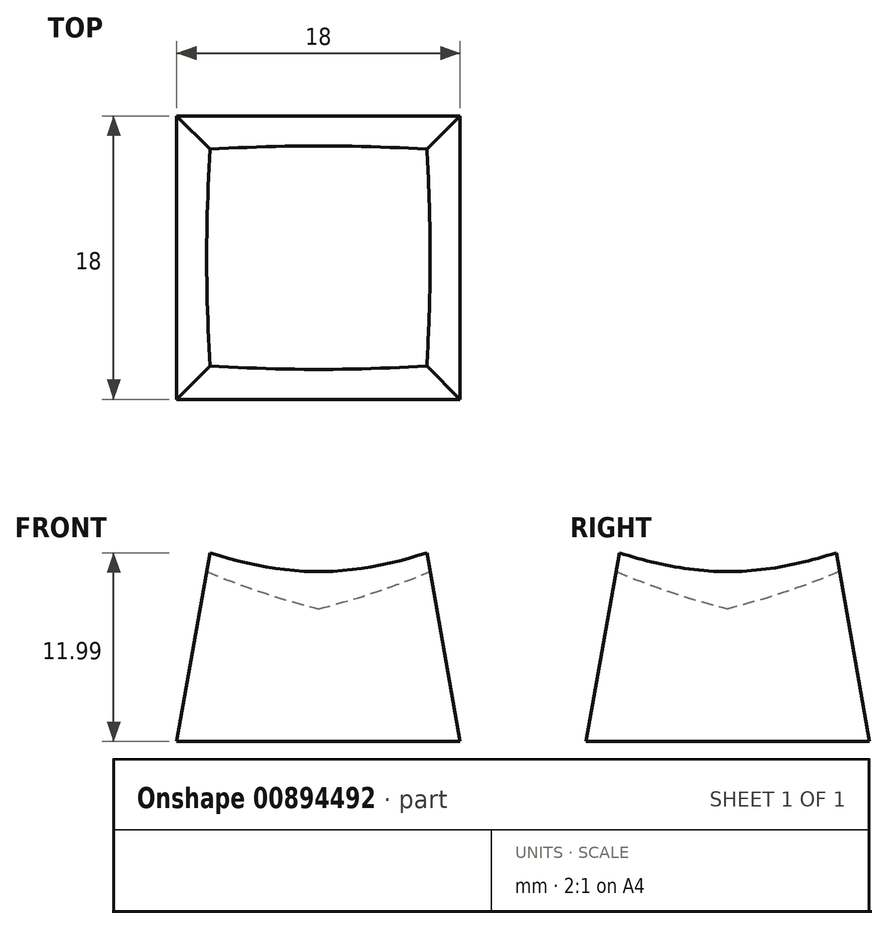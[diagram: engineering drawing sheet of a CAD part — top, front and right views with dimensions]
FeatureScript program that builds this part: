
annotation { "Feature Type Name" : "Feature", "Feature Type Description" : "" }
export const myFeature = defineFeature(function(context is Context, id is Id, definition is map)
    precondition{}
    {
        {
            var Q0;
            Q0=qCreatedBy(makeId("Top.planeOp"),FACE);
            var sketch = newSketch(context, id + "F0", { "sketchPlane" : qUnion([Q0])});
            skLineSegment(sketch, "E0.bottom", {"start": v(-9, 9) * mm, "end": v(9, 9) * mm});
            skLineSegment(sketch, "E0.top", {"start": v(-9, -9) * mm, "end": v(9, -9) * mm});
            skLineSegment(sketch, "E0.left", {"start": v(-9, 9) * mm, "end": v(-9, -9) * mm});
            skLineSegment(sketch, "E0.right", {"start": v(9, 9) * mm, "end": v(9, -9) * mm});
            skPoint(sketch, "E0.middle", {"position": v(0, 0) * mm});
            skSolve(sketch);
        }
        {
            var Q0;
            Q0 = qSketchRegion(id + "F0", true);
            extrude(context, id + "F1", {"entities" : qUnion([Q0]), "depth" : 12 * mm, "offsetDistance" : 25 * mm, "hasDraft" : true, "draftAngle" : 10 * degree, "draftPullDirection" : true});
        }
        {
            var Q0;
            Q0=qCreatedBy(makeId("Right.planeOp"),FACE);
            cPlane(context, id + "F2", {"entities" : qUnion([Q0]), "cplaneType" : CPlaneType.OFFSET, "offset" : 0 * mm, "width" : 150 * mm, "height" : 150 * mm});
        }
        {
            var Q0;
            Q0=qCreatedBy(id+"F2.planeOp",FACE);
            var sketch = newSketch(context, id + "F3", { "sketchPlane" : qUnion([Q0])});
            skArc(sketch, "E1", {"start": v(0, 8.44) * mm, "mid": v(8.34, 11.34) * mm, "end": v(16.03, 15.66) * mm});
            skPoint(sketch, "E2.orphan", {"position": v(6.88, 12) * mm});
            skLineSegment(sketch, "E3", {"start": v(0, 8.44) * mm, "end": v(0, 12) * mm});
            skLineSegment(sketch, "E4", {"start": v(16.03, 15.66) * mm, "end": v(0, 15.66) * mm});
            skLineSegment(sketch, "E5", {"start": v(0, 15.66) * mm, "end": v(0, 12) * mm});
            skPoint(sketch, "E6.orphan", {"position": v(-6.88, 12) * mm});
            skPoint(sketch, "E7.0.start.orphan", {"position": v(9.75, 12) * mm});
            skLineSegment(sketch, "E8", {"start": v(0, 12) * mm, "end": v(0, 8.44) * mm});
            skSolve(sketch);
        }
        {
            var Q0;
            Q0 = qSketchRegion(id + "F3", true);
            var Q1;
            Q1=sQuery(id+"F3.wireOp",EDGE,"E5");
            revolve(context, id + "F4", {"operationType" : NewBodyOperationType.REMOVE, "surfaceOperationType" : NewSurfaceOperationType.NEW, "entities" : qUnion([Q0]), "axis" : qUnion([Q1]), "revolveType" : RevolveType.FULL, "oppositeDirection" : true});
        }
    });
